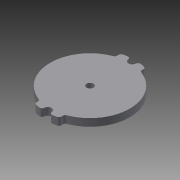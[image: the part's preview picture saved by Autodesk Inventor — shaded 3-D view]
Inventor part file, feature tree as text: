
AUTODESK INVENTOR PART (.ipt)
format: ipt  version: 2013 SP1 (Build 170176100, 176)  size: 115,712 bytes
history: native  units: mm
features: extrude x1
ambient origin geometry x8: Origin, YZ Plane, XZ Plane, XY Plane, X Axis, Y Axis, Z Axis, Center Point
bodies: Solid1 (feature_tree)
feature tree (1):
  extrude  "Extrusion1"  Depth=32.0mm
